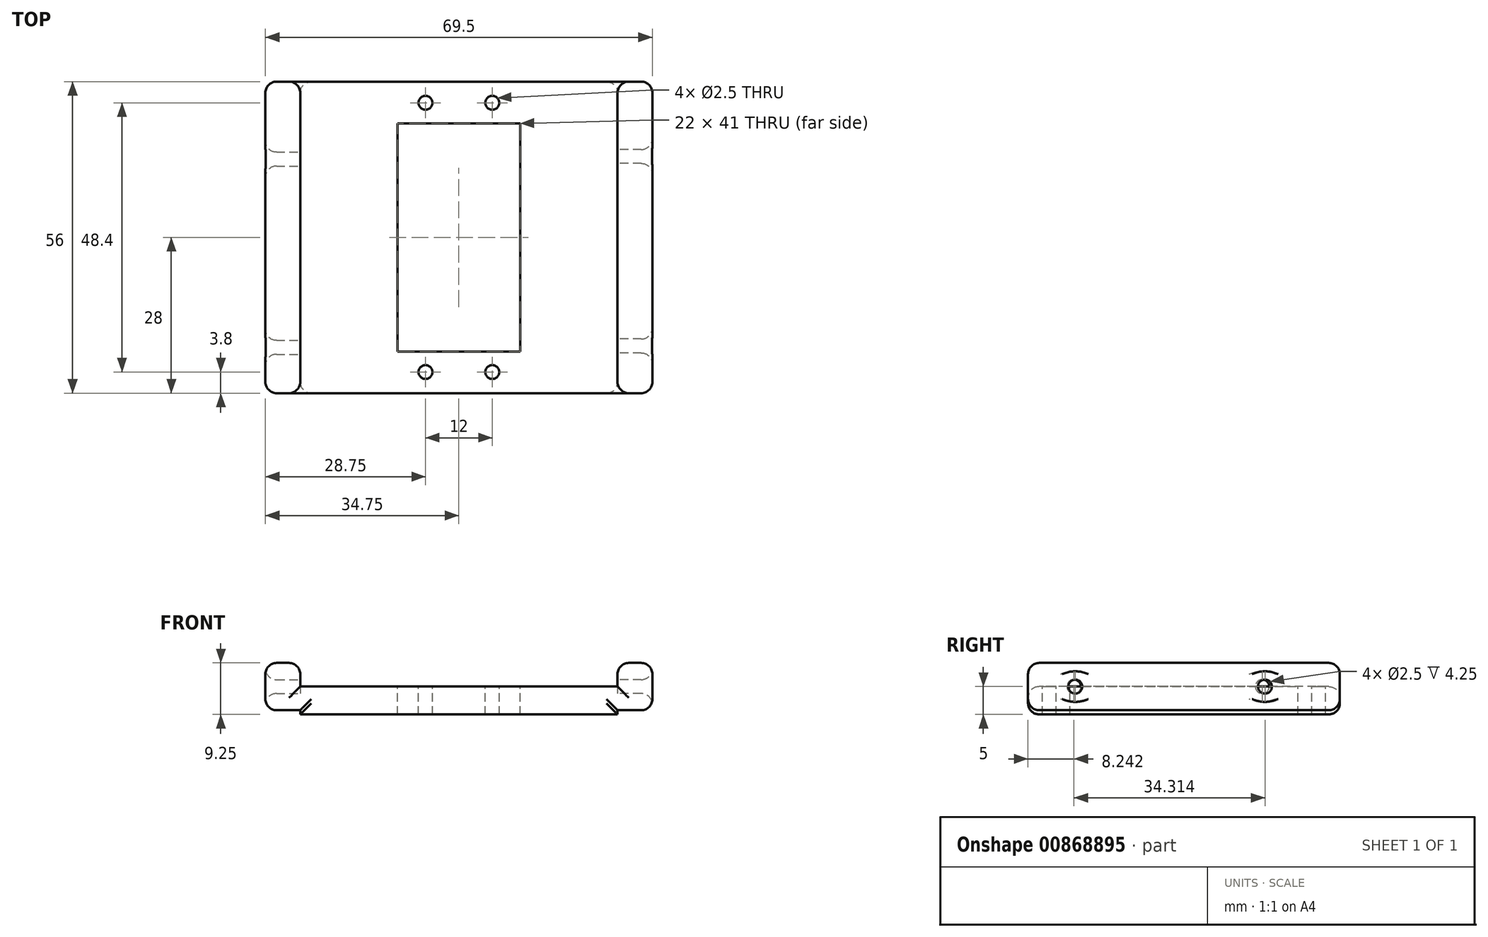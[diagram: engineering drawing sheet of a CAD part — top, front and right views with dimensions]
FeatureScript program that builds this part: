
annotation { "Feature Type Name" : "Feature", "Feature Type Description" : "" }
export const myFeature = defineFeature(function(context is Context, id is Id, definition is map)
    precondition{}
    {
        {
            var Q0;
            Q0=qCreatedBy(makeId("Top.planeOp"),FACE);
            var sketch = newSketch(context, id + "F0", { "sketchPlane" : qUnion([Q0])});
            skLineSegment(sketch, "E0.bottom", {"start": v(34.75, -28) * mm, "end": v(-34.75, -28) * mm});
            skLineSegment(sketch, "E0.top", {"start": v(34.75, 28) * mm, "end": v(-34.75, 28) * mm});
            skLineSegment(sketch, "E0.left", {"start": v(34.75, -28) * mm, "end": v(34.75, 28) * mm});
            skLineSegment(sketch, "E0.right", {"start": v(-34.75, -28) * mm, "end": v(-34.75, 28) * mm});
            skPoint(sketch, "E0.middle", {"position": v(0, 0) * mm});
            skLineSegment(sketch, "E1", {"start": v(-28.5, 28) * mm, "end": v(-28.5, -28) * mm});
            skLineSegment(sketch, "E2", {"start": v(28.5, 28) * mm, "end": v(28.5, -28) * mm});
            skLineSegment(sketch, "E3.bottom", {"start": v(11, -20.5) * mm, "end": v(-11, -20.5) * mm});
            skLineSegment(sketch, "E3.top", {"start": v(11, 20.5) * mm, "end": v(-11, 20.5) * mm});
            skLineSegment(sketch, "E3.left", {"start": v(11, -20.5) * mm, "end": v(11, 20.5) * mm});
            skLineSegment(sketch, "E3.right", {"start": v(-11, -20.5) * mm, "end": v(-11, 20.5) * mm});
            skPoint(sketch, "E4", {"position": v(-6, 24.2) * mm});
            skPoint(sketch, "E5", {"position": v(6, 24.2) * mm});
            skPoint(sketch, "E6", {"position": v(6, -24.2) * mm});
            skPoint(sketch, "E7", {"position": v(-6, -24.2) * mm});
            skSolve(sketch);
        }
        {
            var Q0;
            {var subQ0=sQuery(id+"F0.wireOp",EDGE,"E1");Q0=makeQuery(id+"F0.imprint","IMPRINT",FACE,{"disambiguationData":[TD([[makeQuery(id+"F0.imprint","IMPRINT",EDGE,{"derivedFrom":subQ0}),1.0]])]});}
            extrude(context, id + "F1", {"entities" : qUnion([Q0]), "oppositeDirection" : true, "depth" : 5 * mm, "offsetDistance" : 25 * mm});
        }
        {
            var Q0;
            Q0=makeQuery(id+"F1.opExtrude","SWEPT_FACE",FACE,{"disambiguationData":[OSD([sQuery(id+"F0.wireOp",EDGE,"E1")])]});
            cPlane(context, id + "F2", {"entities" : qUnion([Q0]), "cplaneType" : CPlaneType.OFFSET, "offset" : 0 * mm, "width" : 150 * mm, "height" : 150 * mm});
        }
        {
            var Q0;
            Q0=qCreatedBy(id+"F2.planeOp",FACE);
            var sketch = newSketch(context, id + "F3", { "sketchPlane" : qUnion([Q0])});
            skLineSegment(sketch, "E8.bottom", {"start": v(28, -4.25) * mm, "end": v(-28, -4.25) * mm});
            skLineSegment(sketch, "E8.top", {"start": v(28, 4.25) * mm, "end": v(-28, 4.25) * mm});
            skLineSegment(sketch, "E8.left", {"start": v(28, -4.25) * mm, "end": v(28, 4.25) * mm});
            skLineSegment(sketch, "E8.right", {"start": v(-28, -4.25) * mm, "end": v(-28, 4.25) * mm});
            skPoint(sketch, "E8.middle", {"position": v(0, 0) * mm});
            skPoint(sketch, "E9", {"position": v(-14.08, 0) * mm});
            skPoint(sketch, "E10", {"position": v(19.76, 0) * mm});
            skSolve(sketch);
        }
        {
            var Q0;
            Q0=makeQuery(id+"F3.imprint","IMPRINT",FACE,{"disambiguationData":[TD([[makeQuery(id+"F3.imprint","IMPRINT",EDGE,{"derivedFrom":sQuery(id+"F3.wireOp",EDGE,"E8.bottom")}),-1.0]])]});
            extrude(context, id + "F4", {"entities" : qUnion([Q0]), "operationType" : NewBodyOperationType.ADD, "depth" : 6.25 * mm, "offsetDistance" : 25 * mm});
        }
        {
            var Q0;
            Q0=makeQuery(id+"F1.opExtrude","SWEPT_FACE",FACE,{"disambiguationData":[OSD([sQuery(id+"F0.wireOp",EDGE,"E2")])]});
            cPlane(context, id + "F5", {"entities" : qUnion([Q0]), "cplaneType" : CPlaneType.OFFSET, "offset" : 0 * mm, "width" : 150 * mm, "height" : 150 * mm});
        }
        {
            var Q0;
            Q0=qCreatedBy(id+"F5.planeOp",FACE);
            var sketch = newSketch(context, id + "F6", { "sketchPlane" : qUnion([Q0])});
            skLineSegment(sketch, "E11.bottom", {"start": v(28, -4.25) * mm, "end": v(-28, -4.25) * mm});
            skLineSegment(sketch, "E11.top", {"start": v(28, 4.25) * mm, "end": v(-28, 4.25) * mm});
            skLineSegment(sketch, "E11.left", {"start": v(28, -4.25) * mm, "end": v(28, 4.25) * mm});
            skLineSegment(sketch, "E11.right", {"start": v(-28, -4.25) * mm, "end": v(-28, 4.25) * mm});
            skPoint(sketch, "E11.middle", {"position": v(0, 0) * mm});
            skPoint(sketch, "E12", {"position": v(-19.52, 0) * mm});
            skPoint(sketch, "E13", {"position": v(14.56, 0) * mm});
            skSolve(sketch);
        }
        {
            var Q0;
            Q0=makeQuery(id+"F6.imprint","IMPRINT",FACE,{"disambiguationData":[TD([[makeQuery(id+"F6.imprint","IMPRINT",EDGE,{"derivedFrom":sQuery(id+"F6.wireOp",EDGE,"E11.bottom")}),-1.0]])]});
            extrude(context, id + "F7", {"entities" : qUnion([Q0]), "operationType" : NewBodyOperationType.ADD, "depth" : 6.25 * mm, "offsetDistance" : 25 * mm});
        }
        {
            var Q0;
            Q0=sQuery(id+"F0.wireOp",VERTEX,"E5");
            var Q1;
            Q1=sQuery(id+"F0.wireOp",VERTEX,"E4");
            var Q2;
            Q2=sQuery(id+"F0.wireOp",VERTEX,"E7");
            var Q3;
            Q3=sQuery(id+"F0.wireOp",VERTEX,"E6");
            var Q4;
            Q4=makeQuery(id+"F1.opExtrude","SWEPT_BODY",BODY,{"disambiguationData":[OSD([sQuery(id+"F0.wireOp",EDGE,"E0.bottom"),sQuery(id+"F0.wireOp",EDGE,"E0.top"),sQuery(id+"F0.wireOp",EDGE,"E1"),sQuery(id+"F0.wireOp",EDGE,"E2"),sQuery(id+"F0.wireOp",EDGE,"E3.bottom"),sQuery(id+"F0.wireOp",EDGE,"E3.top"),sQuery(id+"F0.wireOp",EDGE,"E3.left"),sQuery(id+"F0.wireOp",EDGE,"E3.right")])]});
            hole(context, id + "F8", {"style" : HoleStyle.SIMPLE, "endStyle" : HoleEndStyle.THROUGH, "standardTappedOrClearance" : lookupTablePath({ "standard" : "ISO", "engagement" : "75%", "pitch" : "0.5 mm", "size" : "M3", "type" : "Tapped" }), "standardBlindInLast" : lookupTablePath({ "standard" : "ISO", "engagement" : "75%", "pitch" : "0.5 mm", "size" : "M3", "type" : "Tapped" }), "holeDiameter" : 2.5 * mm, "majorDiameter" : 3 * mm, "showTappedDepth" : true, "isTappedThrough" : true, "tappedDepth" : 12 * mm, "tapClearance" : 3, "startFromSketch" : true, "locations" : qUnion([Q0, Q1, Q2, Q3]), "scope" : qUnion([Q4])});
        }
        {
            var Q0;
            Q0=sQuery(id+"F3.wireOp",VERTEX,"E9");
            var Q1;
            Q1=sQuery(id+"F3.wireOp",VERTEX,"E10");
            var Q2;
            Q2=makeQuery(id+"F1.opExtrude","SWEPT_BODY",BODY,{"disambiguationData":[OSD([sQuery(id+"F0.wireOp",EDGE,"E0.bottom"),sQuery(id+"F0.wireOp",EDGE,"E0.top"),sQuery(id+"F0.wireOp",EDGE,"E1"),sQuery(id+"F0.wireOp",EDGE,"E2"),sQuery(id+"F0.wireOp",EDGE,"E3.bottom"),sQuery(id+"F0.wireOp",EDGE,"E3.top"),sQuery(id+"F0.wireOp",EDGE,"E3.left"),sQuery(id+"F0.wireOp",EDGE,"E3.right")])]});
            hole(context, id + "F9", {"style" : HoleStyle.SIMPLE, "endStyle" : HoleEndStyle.THROUGH, "oppositeDirection" : true, "standardTappedOrClearance" : lookupTablePath({ "standard" : "ISO", "engagement" : "75%", "pitch" : "0.5 mm", "size" : "M3", "type" : "Tapped" }), "standardBlindInLast" : lookupTablePath({ "standard" : "ISO", "engagement" : "75%", "pitch" : "0.5 mm", "size" : "M3", "type" : "Tapped" }), "holeDiameter" : 2.5 * mm, "majorDiameter" : 3 * mm, "showTappedDepth" : true, "isTappedThrough" : true, "tappedDepth" : 12 * mm, "tapClearance" : 3, "startFromSketch" : true, "locations" : qUnion([Q0, Q1]), "scope" : qUnion([Q2])});
        }
        {
            var Q0;
            Q0=sQuery(id+"F6.wireOp",VERTEX,"E12");
            var Q1;
            Q1=sQuery(id+"F6.wireOp",VERTEX,"E13");
            var Q2;
            Q2=makeQuery(id+"F1.opExtrude","SWEPT_BODY",BODY,{"disambiguationData":[OSD([sQuery(id+"F0.wireOp",EDGE,"E0.bottom"),sQuery(id+"F0.wireOp",EDGE,"E0.top"),sQuery(id+"F0.wireOp",EDGE,"E1"),sQuery(id+"F0.wireOp",EDGE,"E2"),sQuery(id+"F0.wireOp",EDGE,"E3.bottom"),sQuery(id+"F0.wireOp",EDGE,"E3.top"),sQuery(id+"F0.wireOp",EDGE,"E3.left"),sQuery(id+"F0.wireOp",EDGE,"E3.right")])]});
            hole(context, id + "F10", {"style" : HoleStyle.SIMPLE, "endStyle" : HoleEndStyle.THROUGH, "oppositeDirection" : true, "standardTappedOrClearance" : lookupTablePath({ "standard" : "ISO", "engagement" : "75%", "pitch" : "0.5 mm", "size" : "M3", "type" : "Tapped" }), "standardBlindInLast" : lookupTablePath({ "standard" : "ISO", "engagement" : "75%", "pitch" : "0.5 mm", "size" : "M3", "type" : "Tapped" }), "holeDiameter" : 2.5 * mm, "majorDiameter" : 3 * mm, "showTappedDepth" : true, "isTappedThrough" : true, "tappedDepth" : 12 * mm, "tapClearance" : 3, "startFromSketch" : true, "locations" : qUnion([Q0, Q1]), "scope" : qUnion([Q2])});
        }
        {
            var Q0;
            Q0=makeQuery(id+"F7.opExtrude","SWEPT_FACE",FACE,{"disambiguationData":[OSD([sQuery(id+"F6.wireOp",EDGE,"E11.top")])]});
            var Q1;
            Q1=makeQuery(id+"F7.opExtrude","CAP_FACE",FACE,{"disambiguationData":[OSD([sQuery(id+"F6.wireOp",EDGE,"E11.bottom"),sQuery(id+"F6.wireOp",EDGE,"E11.top"),sQuery(id+"F6.wireOp",EDGE,"E11.left"),sQuery(id+"F6.wireOp",EDGE,"E11.right")])],"isStart":false});
            var Q2;
            Q2=makeQuery(id+"F7.boolean.opBoolean","MERGE",FACE,{"derivedFrom":[makeQuery(id+"F4.boolean.opBoolean","MERGE",FACE,{"derivedFrom":[makeQuery(id+"F1.opExtrude","SWEPT_FACE",FACE,{"disambiguationData":[OSD([sQuery(id+"F0.wireOp",EDGE,"E0.bottom")])]}),makeQuery(id+"F4.opExtrude","SWEPT_FACE",FACE,{"disambiguationData":[OSD([sQuery(id+"F3.wireOp",EDGE,"E8.left")])]})]}),makeQuery(id+"F7.opExtrude","SWEPT_FACE",FACE,{"disambiguationData":[OSD([sQuery(id+"F6.wireOp",EDGE,"E11.right")])]})]});
            var Q3;
            Q3=makeQuery(id+"F7.boolean.opBoolean","MERGE",FACE,{"derivedFrom":[makeQuery(id+"F4.boolean.opBoolean","MERGE",FACE,{"derivedFrom":[makeQuery(id+"F1.opExtrude","SWEPT_FACE",FACE,{"disambiguationData":[OSD([sQuery(id+"F0.wireOp",EDGE,"E0.top")])]}),makeQuery(id+"F4.opExtrude","SWEPT_FACE",FACE,{"disambiguationData":[OSD([sQuery(id+"F3.wireOp",EDGE,"E8.right")])]})]}),makeQuery(id+"F7.opExtrude","SWEPT_FACE",FACE,{"disambiguationData":[OSD([sQuery(id+"F6.wireOp",EDGE,"E11.left")])]})]});
            var Q4;
            Q4=makeQuery(id+"F4.opExtrude","SWEPT_FACE",FACE,{"disambiguationData":[OSD([sQuery(id+"F3.wireOp",EDGE,"E8.top")])]});
            var Q5;
            Q5=makeQuery(id+"F4.opExtrude","CAP_FACE",FACE,{"disambiguationData":[OSD([sQuery(id+"F3.wireOp",EDGE,"E8.bottom"),sQuery(id+"F3.wireOp",EDGE,"E8.top"),sQuery(id+"F3.wireOp",EDGE,"E8.left"),sQuery(id+"F3.wireOp",EDGE,"E8.right")])],"isStart":false});
            fillet(context, id + "F11", {"entities" : qUnion([Q0, Q1, Q2, Q3, Q4, Q5]), "radius" : 2 * mm, "tangentPropagation" : true, "allowEdgeOverflow" : false});
        }
    });
